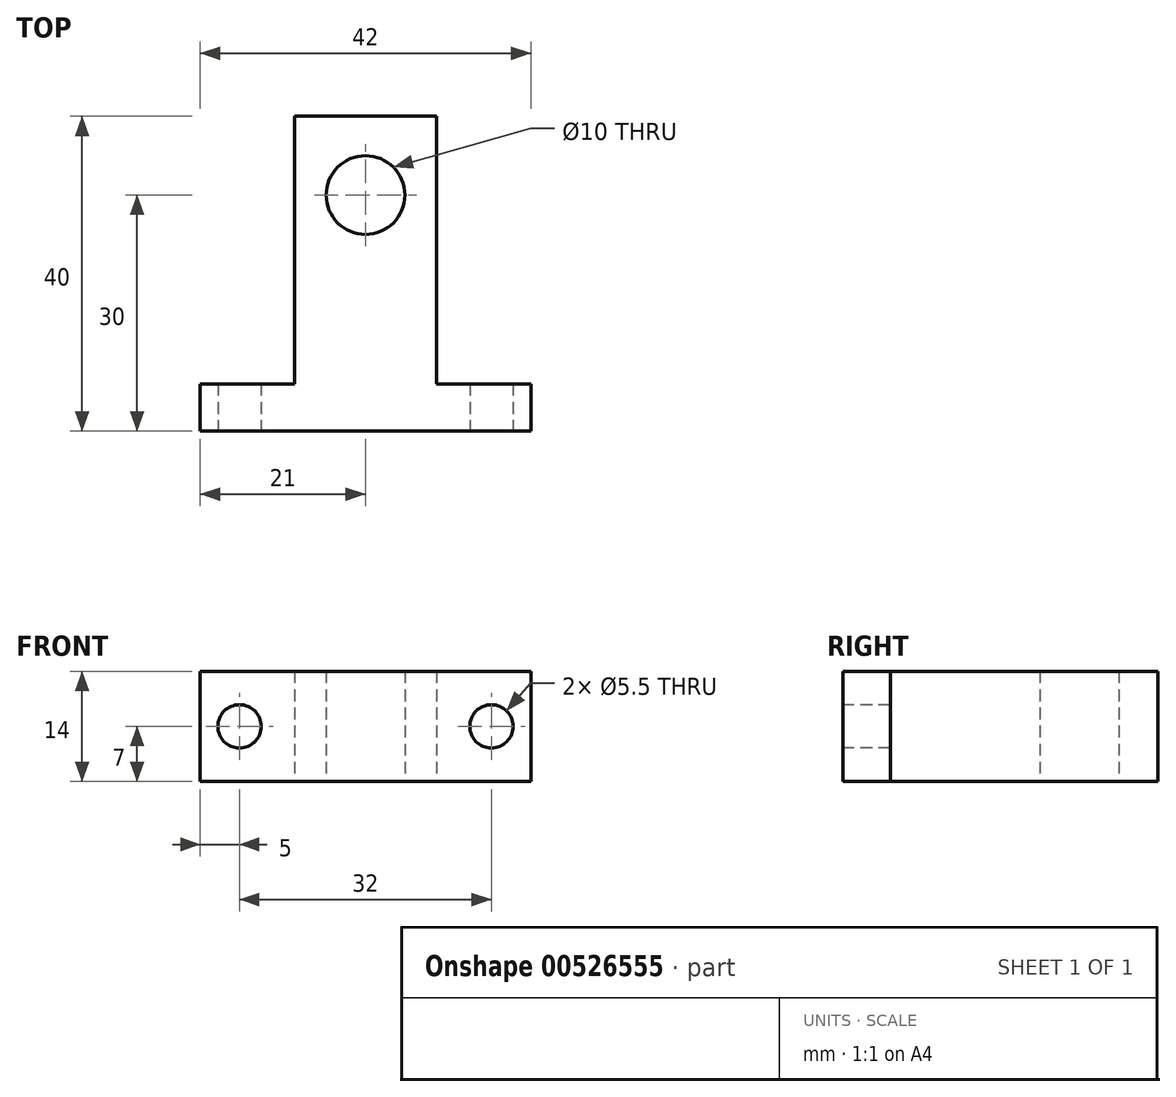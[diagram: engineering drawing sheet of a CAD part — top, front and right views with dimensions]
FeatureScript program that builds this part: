
annotation { "Feature Type Name" : "Feature", "Feature Type Description" : "" }
export const myFeature = defineFeature(function(context is Context, id is Id, definition is map)
    precondition{}
    {
        {
            var Q0;
            Q0=qCreatedBy(makeId("Top.planeOp"),FACE);
            var sketch = newSketch(context, id + "F0", { "sketchPlane" : qUnion([Q0])});
            skLineSegment(sketch, "E0", {"start": v(-9, 40) * mm, "end": v(9, 40) * mm});
            skLineSegment(sketch, "E1", {"start": v(9, 40) * mm, "end": v(9, 6) * mm});
            skLineSegment(sketch, "E2", {"start": v(9, 6) * mm, "end": v(21, 6) * mm});
            skLineSegment(sketch, "E3", {"start": v(21, 6) * mm, "end": v(21, 0) * mm});
            skLineSegment(sketch, "E4", {"start": v(21, 0) * mm, "end": v(-21, 0) * mm});
            skLineSegment(sketch, "E5", {"start": v(-21, 0) * mm, "end": v(-21, 6) * mm});
            skLineSegment(sketch, "E6", {"start": v(-21, 6) * mm, "end": v(-9, 6) * mm});
            skLineSegment(sketch, "E7", {"start": v(-9, 6) * mm, "end": v(-9, 40) * mm});
            skCircle(sketch, "E8", {"center": v(0, 30) * mm, "radius": 5 * mm});
            skSolve(sketch);
        }
        {
            var Q0;
            Q0=qSketchRegion(id+"F0",true);
            extrude(context, id + "F1", {"entities" : qUnion([Q0]), "depth" : 14 * mm, "offsetDistance" : 25 * mm});
        }
        {
            var Q0;
            Q0=qCreatedBy(makeId("Front.planeOp"),FACE);
            var sketch = newSketch(context, id + "F2", { "sketchPlane" : qUnion([Q0])});
            skCircle(sketch, "E9", {"center": v(-16, 7) * mm, "radius": 2.75 * mm});
            skCircle(sketch, "E10.MirrorC", {"center": v(16, 7) * mm, "radius": 2.75 * mm});
            skSolve(sketch);
        }
        {
            var Q0;
            Q0=qSketchRegion(id+"F2",true);
            extrude(context, id + "F3", {"entities" : qUnion([Q0]), "operationType" : NewBodyOperationType.REMOVE, "oppositeDirection" : true, "depth" : 6 * mm, "offsetDistance" : 25 * mm});
        }
    });
